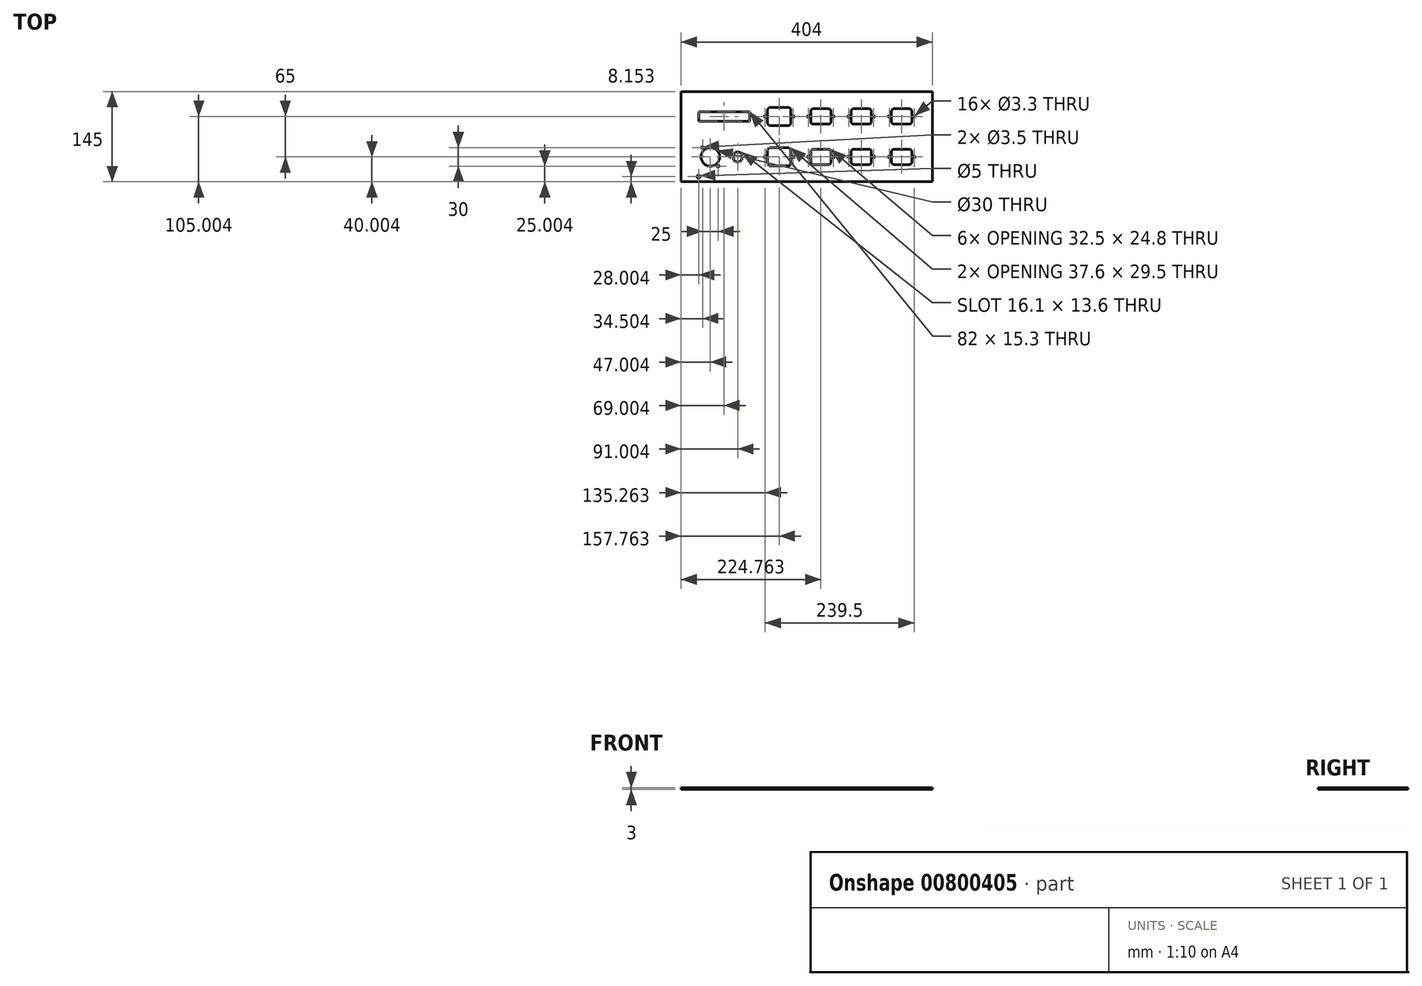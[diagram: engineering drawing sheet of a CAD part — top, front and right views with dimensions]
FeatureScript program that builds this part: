
annotation { "Feature Type Name" : "Feature", "Feature Type Description" : "" }
export const myFeature = defineFeature(function(context is Context, id is Id, definition is map)
    precondition{}
    {
        {
            var Q0;
            Q0=qCreatedBy(makeId("Top.planeOp"),FACE);
            var sketch = newSketch(context, id + "F0", { "sketchPlane" : qUnion([Q0])});
            skLineSegment(sketch, "E0.bottom", {"start": v(-216.19, 64.87) * mm, "end": v(187.81, 64.87) * mm});
            skLineSegment(sketch, "E0.top", {"start": v(-216.19, -80.13) * mm, "end": v(187.81, -80.13) * mm});
            skLineSegment(sketch, "E0.left", {"start": v(-216.19, 64.87) * mm, "end": v(-216.19, -80.13) * mm});
            skLineSegment(sketch, "E0.right", {"start": v(187.81, 64.87) * mm, "end": v(187.81, -80.13) * mm});
            skSolve(sketch);
        }
        {
            var Q0;
            Q0=qCreatedBy(makeId("Top.planeOp"),FACE);
            var sketch = newSketch(context, id + "F1", { "sketchPlane" : qUnion([Q0])});
            skLineSegment(sketch, "E1.bottom", {"start": v(150.82, 12.47) * mm, "end": v(126.32, 12.47) * mm});
            skLineSegment(sketch, "E1.top", {"start": v(150.82, 37.27) * mm, "end": v(126.32, 37.27) * mm});
            skLineSegment(sketch, "E1.left", {"start": v(154.82, 16.47) * mm, "end": v(154.82, 33.27) * mm});
            skLineSegment(sketch, "E1.right", {"start": v(122.32, 16.47) * mm, "end": v(122.32, 33.27) * mm});
            skPoint(sketch, "E1.middle", {"position": v(138.57, 24.87) * mm});
            skPoint(sketch, "E2.visualSharp", {"position": v(122.32, 37.27) * mm});
            skArc(sketch, "E2.filletArc", {"start": v(126.32, 37.27) * mm, "mid": v(123.5, 36.1) * mm, "end": v(122.32, 33.27) * mm});
            skPoint(sketch, "E3.visualSharp", {"position": v(154.82, 37.27) * mm});
            skArc(sketch, "E3.filletArc", {"start": v(154.82, 33.27) * mm, "mid": v(153.65, 36.1) * mm, "end": v(150.82, 37.27) * mm});
            skPoint(sketch, "E4.visualSharp", {"position": v(154.82, 12.47) * mm});
            skArc(sketch, "E4.filletArc", {"start": v(150.82, 12.47) * mm, "mid": v(153.65, 13.65) * mm, "end": v(154.82, 16.47) * mm});
            skPoint(sketch, "E5.visualSharp", {"position": v(122.32, 12.47) * mm});
            skArc(sketch, "E5.filletArc", {"start": v(122.32, 16.47) * mm, "mid": v(123.5, 13.65) * mm, "end": v(126.32, 12.47) * mm});
            skCircle(sketch, "E6", {"center": v(158.57, 24.87) * mm, "radius": 1.5 * mm});
            skCircle(sketch, "E7", {"center": v(118.57, 24.87) * mm, "radius": 1.5 * mm});
            skLineSegment(sketch, "E8.bottom", {"start": v(-44.63, 10.12) * mm, "end": v(-72.23, 10.12) * mm});
            skLineSegment(sketch, "E8.top", {"start": v(-44.63, 39.62) * mm, "end": v(-72.23, 39.62) * mm});
            skLineSegment(sketch, "E8.left", {"start": v(-39.63, 15.12) * mm, "end": v(-39.63, 34.62) * mm});
            skLineSegment(sketch, "E8.right", {"start": v(-77.23, 15.12) * mm, "end": v(-77.23, 34.62) * mm});
            skPoint(sketch, "E8.middle", {"position": v(-58.43, 24.87) * mm});
            skPoint(sketch, "E9.visualSharp", {"position": v(-77.23, 39.62) * mm});
            skArc(sketch, "E9.filletArc", {"start": v(-72.23, 39.62) * mm, "mid": v(-75.76, 38.16) * mm, "end": v(-77.23, 34.62) * mm});
            skPoint(sketch, "E10.visualSharp", {"position": v(-39.63, 39.62) * mm});
            skArc(sketch, "E10.filletArc", {"start": v(-39.63, 34.62) * mm, "mid": v(-41.1, 38.16) * mm, "end": v(-44.63, 39.62) * mm});
            skPoint(sketch, "E11.visualSharp", {"position": v(-39.63, 10.12) * mm});
            skArc(sketch, "E11.filletArc", {"start": v(-44.63, 10.12) * mm, "mid": v(-41.1, 11.59) * mm, "end": v(-39.63, 15.12) * mm});
            skPoint(sketch, "E12.visualSharp", {"position": v(-77.23, 10.12) * mm});
            skArc(sketch, "E12.filletArc", {"start": v(-77.23, 15.12) * mm, "mid": v(-75.76, 11.59) * mm, "end": v(-72.23, 10.12) * mm});
            skCircle(sketch, "E13", {"center": v(-35.93, 24.87) * mm, "radius": 1.5 * mm});
            skCircle(sketch, "E14", {"center": v(-80.93, 24.87) * mm, "radius": 1.5 * mm});
            skLineSegment(sketch, "E15", {"start": v(-85.43, 7.87) * mm, "end": v(-85.43, 41.87) * mm, "construction": true});
            skLineSegment(sketch, "E16", {"start": v(-85.43, 41.87) * mm, "end": v(-31.43, 41.87) * mm, "construction": true});
            skLineSegment(sketch, "E17", {"start": v(-31.43, 41.87) * mm, "end": v(-31.43, 7.87) * mm, "construction": true});
            skLineSegment(sketch, "E18", {"start": v(-31.43, 7.87) * mm, "end": v(-85.43, 7.87) * mm, "construction": true});
            skLineSegment(sketch, "E19", {"start": v(113.57, 38.87) * mm, "end": v(113.57, 10.87) * mm, "construction": true});
            skLineSegment(sketch, "E20", {"start": v(113.57, 10.87) * mm, "end": v(163.57, 10.87) * mm, "construction": true});
            skLineSegment(sketch, "E21", {"start": v(163.57, 10.87) * mm, "end": v(163.57, 38.87) * mm, "construction": true});
            skLineSegment(sketch, "E22", {"start": v(163.57, 38.87) * mm, "end": v(113.57, 38.87) * mm, "construction": true});
            skLineSegment(sketch, "E23.0.1.0", {"start": v(163.57, -26.13) * mm, "end": v(113.57, -26.13) * mm, "construction": true});
            skLineSegment(sketch, "E23.0.1.1", {"start": v(113.57, -26.13) * mm, "end": v(113.57, -54.13) * mm, "construction": true});
            skLineSegment(sketch, "E23.0.1.2", {"start": v(163.57, -54.13) * mm, "end": v(163.57, -26.13) * mm, "construction": true});
            skLineSegment(sketch, "E23.0.1.3", {"start": v(122.32, -48.53) * mm, "end": v(122.32, -31.73) * mm});
            skLineSegment(sketch, "E23.0.1.4", {"start": v(154.82, -48.53) * mm, "end": v(154.82, -31.73) * mm});
            skLineSegment(sketch, "E23.0.1.5", {"start": v(150.82, -27.73) * mm, "end": v(126.32, -27.73) * mm});
            skPoint(sketch, "E23.0.1.6", {"position": v(154.82, -27.73) * mm});
            skLineSegment(sketch, "E23.0.1.7", {"start": v(150.82, -52.53) * mm, "end": v(126.32, -52.53) * mm});
            skLineSegment(sketch, "E23.0.1.8", {"start": v(113.57, -54.13) * mm, "end": v(163.57, -54.13) * mm, "construction": true});
            skPoint(sketch, "E23.0.1.9", {"position": v(138.57, -40.13) * mm});
            skPoint(sketch, "E23.0.1.10", {"position": v(122.32, -52.53) * mm});
            skPoint(sketch, "E23.0.1.11", {"position": v(154.82, -52.53) * mm});
            skPoint(sketch, "E23.0.1.12", {"position": v(122.32, -27.73) * mm});
            skCircle(sketch, "E23.0.1.13", {"center": v(158.57, -40.13) * mm, "radius": 1.5 * mm});
            skCircle(sketch, "E23.0.1.14", {"center": v(118.57, -40.13) * mm, "radius": 1.5 * mm});
            skArc(sketch, "E23.0.1.15", {"start": v(122.32, -48.53) * mm, "mid": v(123.5, -51.35) * mm, "end": v(126.32, -52.53) * mm});
            skArc(sketch, "E23.0.1.16", {"start": v(154.82, -31.73) * mm, "mid": v(153.65, -28.9) * mm, "end": v(150.82, -27.73) * mm});
            skArc(sketch, "E23.0.1.17", {"start": v(150.82, -52.53) * mm, "mid": v(153.65, -51.35) * mm, "end": v(154.82, -48.53) * mm});
            skArc(sketch, "E23.0.1.18", {"start": v(126.32, -27.73) * mm, "mid": v(123.5, -28.9) * mm, "end": v(122.32, -31.73) * mm});
            skLineSegment(sketch, "E23.1.0.0", {"start": v(98.57, 38.87) * mm, "end": v(48.57, 38.87) * mm, "construction": true});
            skLineSegment(sketch, "E23.1.0.1", {"start": v(48.57, 38.87) * mm, "end": v(48.57, 10.87) * mm, "construction": true});
            skLineSegment(sketch, "E23.1.0.2", {"start": v(98.57, 10.87) * mm, "end": v(98.57, 38.87) * mm, "construction": true});
            skLineSegment(sketch, "E23.1.0.3", {"start": v(57.32, 16.47) * mm, "end": v(57.32, 33.27) * mm});
            skLineSegment(sketch, "E23.1.0.4", {"start": v(89.82, 16.47) * mm, "end": v(89.82, 33.27) * mm});
            skLineSegment(sketch, "E23.1.0.5", {"start": v(85.82, 37.27) * mm, "end": v(61.32, 37.27) * mm});
            skPoint(sketch, "E23.1.0.6", {"position": v(89.82, 37.27) * mm});
            skLineSegment(sketch, "E23.1.0.7", {"start": v(85.82, 12.47) * mm, "end": v(61.32, 12.47) * mm});
            skLineSegment(sketch, "E23.1.0.8", {"start": v(48.57, 10.87) * mm, "end": v(98.57, 10.87) * mm, "construction": true});
            skPoint(sketch, "E23.1.0.9", {"position": v(73.57, 24.87) * mm});
            skPoint(sketch, "E23.1.0.10", {"position": v(57.32, 12.47) * mm});
            skPoint(sketch, "E23.1.0.11", {"position": v(89.82, 12.47) * mm});
            skPoint(sketch, "E23.1.0.12", {"position": v(57.32, 37.27) * mm});
            skCircle(sketch, "E23.1.0.13", {"center": v(93.57, 24.87) * mm, "radius": 1.5 * mm});
            skCircle(sketch, "E23.1.0.14", {"center": v(53.57, 24.87) * mm, "radius": 1.5 * mm});
            skArc(sketch, "E23.1.0.15", {"start": v(57.32, 16.47) * mm, "mid": v(58.5, 13.65) * mm, "end": v(61.32, 12.47) * mm});
            skArc(sketch, "E23.1.0.16", {"start": v(89.82, 33.27) * mm, "mid": v(88.65, 36.1) * mm, "end": v(85.82, 37.27) * mm});
            skArc(sketch, "E23.1.0.17", {"start": v(85.82, 12.47) * mm, "mid": v(88.65, 13.65) * mm, "end": v(89.82, 16.47) * mm});
            skArc(sketch, "E23.1.0.18", {"start": v(61.32, 37.27) * mm, "mid": v(58.5, 36.1) * mm, "end": v(57.32, 33.27) * mm});
            skLineSegment(sketch, "E23.1.1.0", {"start": v(98.57, -26.13) * mm, "end": v(48.57, -26.13) * mm, "construction": true});
            skLineSegment(sketch, "E23.1.1.1", {"start": v(48.57, -26.13) * mm, "end": v(48.57, -54.13) * mm, "construction": true});
            skLineSegment(sketch, "E23.1.1.2", {"start": v(98.57, -54.13) * mm, "end": v(98.57, -26.13) * mm, "construction": true});
            skLineSegment(sketch, "E23.1.1.3", {"start": v(57.32, -48.53) * mm, "end": v(57.32, -31.73) * mm});
            skLineSegment(sketch, "E23.1.1.4", {"start": v(89.82, -48.53) * mm, "end": v(89.82, -31.73) * mm});
            skLineSegment(sketch, "E23.1.1.5", {"start": v(85.82, -27.73) * mm, "end": v(61.32, -27.73) * mm});
            skPoint(sketch, "E23.1.1.6", {"position": v(89.82, -27.73) * mm});
            skLineSegment(sketch, "E23.1.1.7", {"start": v(85.82, -52.53) * mm, "end": v(61.32, -52.53) * mm});
            skLineSegment(sketch, "E23.1.1.8", {"start": v(48.57, -54.13) * mm, "end": v(98.57, -54.13) * mm, "construction": true});
            skPoint(sketch, "E23.1.1.9", {"position": v(73.57, -40.13) * mm});
            skPoint(sketch, "E23.1.1.10", {"position": v(57.32, -52.53) * mm});
            skPoint(sketch, "E23.1.1.11", {"position": v(89.82, -52.53) * mm});
            skPoint(sketch, "E23.1.1.12", {"position": v(57.32, -27.73) * mm});
            skCircle(sketch, "E23.1.1.13", {"center": v(93.57, -40.13) * mm, "radius": 1.5 * mm});
            skCircle(sketch, "E23.1.1.14", {"center": v(53.57, -40.13) * mm, "radius": 1.5 * mm});
            skArc(sketch, "E23.1.1.15", {"start": v(57.32, -48.53) * mm, "mid": v(58.5, -51.35) * mm, "end": v(61.32, -52.53) * mm});
            skArc(sketch, "E23.1.1.16", {"start": v(89.82, -31.73) * mm, "mid": v(88.65, -28.9) * mm, "end": v(85.82, -27.73) * mm});
            skArc(sketch, "E23.1.1.17", {"start": v(85.82, -52.53) * mm, "mid": v(88.65, -51.35) * mm, "end": v(89.82, -48.53) * mm});
            skArc(sketch, "E23.1.1.18", {"start": v(61.32, -27.73) * mm, "mid": v(58.5, -28.9) * mm, "end": v(57.32, -31.73) * mm});
            skLineSegment(sketch, "E23.2.0.0", {"start": v(33.57, 38.87) * mm, "end": v(-16.43, 38.87) * mm, "construction": true});
            skLineSegment(sketch, "E23.2.0.1", {"start": v(-16.43, 38.87) * mm, "end": v(-16.43, 10.87) * mm, "construction": true});
            skLineSegment(sketch, "E23.2.0.2", {"start": v(33.57, 10.87) * mm, "end": v(33.57, 38.87) * mm, "construction": true});
            skLineSegment(sketch, "E23.2.0.3", {"start": v(-7.68, 16.47) * mm, "end": v(-7.68, 33.27) * mm});
            skLineSegment(sketch, "E23.2.0.4", {"start": v(24.82, 16.47) * mm, "end": v(24.82, 33.27) * mm});
            skLineSegment(sketch, "E23.2.0.5", {"start": v(20.82, 37.27) * mm, "end": v(-3.68, 37.27) * mm});
            skPoint(sketch, "E23.2.0.6", {"position": v(24.82, 37.27) * mm});
            skLineSegment(sketch, "E23.2.0.7", {"start": v(20.82, 12.47) * mm, "end": v(-3.68, 12.47) * mm});
            skLineSegment(sketch, "E23.2.0.8", {"start": v(-16.43, 10.87) * mm, "end": v(33.57, 10.87) * mm, "construction": true});
            skPoint(sketch, "E23.2.0.9", {"position": v(8.57, 24.87) * mm});
            skPoint(sketch, "E23.2.0.10", {"position": v(-7.68, 12.47) * mm});
            skPoint(sketch, "E23.2.0.11", {"position": v(24.82, 12.47) * mm});
            skPoint(sketch, "E23.2.0.12", {"position": v(-7.68, 37.27) * mm});
            skCircle(sketch, "E23.2.0.13", {"center": v(28.57, 24.87) * mm, "radius": 1.5 * mm});
            skCircle(sketch, "E23.2.0.14", {"center": v(-11.43, 24.87) * mm, "radius": 1.5 * mm});
            skArc(sketch, "E23.2.0.15", {"start": v(-7.68, 16.47) * mm, "mid": v(-6.5, 13.65) * mm, "end": v(-3.68, 12.47) * mm});
            skArc(sketch, "E23.2.0.16", {"start": v(24.82, 33.27) * mm, "mid": v(23.65, 36.1) * mm, "end": v(20.82, 37.27) * mm});
            skArc(sketch, "E23.2.0.17", {"start": v(20.82, 12.47) * mm, "mid": v(23.65, 13.65) * mm, "end": v(24.82, 16.47) * mm});
            skArc(sketch, "E23.2.0.18", {"start": v(-3.68, 37.27) * mm, "mid": v(-6.5, 36.1) * mm, "end": v(-7.68, 33.27) * mm});
            skLineSegment(sketch, "E23.2.1.0", {"start": v(33.57, -26.13) * mm, "end": v(-16.43, -26.13) * mm, "construction": true});
            skLineSegment(sketch, "E23.2.1.1", {"start": v(-16.43, -26.13) * mm, "end": v(-16.43, -54.13) * mm, "construction": true});
            skLineSegment(sketch, "E23.2.1.2", {"start": v(33.57, -54.13) * mm, "end": v(33.57, -26.13) * mm, "construction": true});
            skLineSegment(sketch, "E23.2.1.3", {"start": v(-7.68, -48.53) * mm, "end": v(-7.68, -31.73) * mm});
            skLineSegment(sketch, "E23.2.1.4", {"start": v(24.82, -48.53) * mm, "end": v(24.82, -31.73) * mm});
            skLineSegment(sketch, "E23.2.1.5", {"start": v(20.82, -27.73) * mm, "end": v(-3.68, -27.73) * mm});
            skPoint(sketch, "E23.2.1.6", {"position": v(24.82, -27.73) * mm});
            skLineSegment(sketch, "E23.2.1.7", {"start": v(20.82, -52.53) * mm, "end": v(-3.68, -52.53) * mm});
            skLineSegment(sketch, "E23.2.1.8", {"start": v(-16.43, -54.13) * mm, "end": v(33.57, -54.13) * mm, "construction": true});
            skPoint(sketch, "E23.2.1.9", {"position": v(8.57, -40.13) * mm});
            skPoint(sketch, "E23.2.1.10", {"position": v(-7.68, -52.53) * mm});
            skPoint(sketch, "E23.2.1.11", {"position": v(24.82, -52.53) * mm});
            skPoint(sketch, "E23.2.1.12", {"position": v(-7.68, -27.73) * mm});
            skCircle(sketch, "E23.2.1.13", {"center": v(28.57, -40.13) * mm, "radius": 1.5 * mm});
            skCircle(sketch, "E23.2.1.14", {"center": v(-11.43, -40.13) * mm, "radius": 1.5 * mm});
            skArc(sketch, "E23.2.1.15", {"start": v(-7.68, -48.53) * mm, "mid": v(-6.5, -51.35) * mm, "end": v(-3.68, -52.53) * mm});
            skArc(sketch, "E23.2.1.16", {"start": v(24.82, -31.73) * mm, "mid": v(23.65, -28.9) * mm, "end": v(20.82, -27.73) * mm});
            skArc(sketch, "E23.2.1.17", {"start": v(20.82, -52.53) * mm, "mid": v(23.65, -51.35) * mm, "end": v(24.82, -48.53) * mm});
            skArc(sketch, "E23.2.1.18", {"start": v(-3.68, -27.73) * mm, "mid": v(-6.5, -28.9) * mm, "end": v(-7.68, -31.73) * mm});
            skLineSegment(sketch, "E23.direction1", {"start": v(113.57, 10.87) * mm, "end": v(48.57, 10.87) * mm, "construction": true});
            skLineSegment(sketch, "E23.direction2", {"start": v(113.57, 10.87) * mm, "end": v(113.57, -54.13) * mm, "construction": true});
            skPoint(sketch, "E24.0.1.0", {"position": v(-77.23, -54.88) * mm});
            skPoint(sketch, "E24.0.1.1", {"position": v(-39.63, -54.88) * mm});
            skLineSegment(sketch, "E24.0.1.2", {"start": v(-85.43, -23.13) * mm, "end": v(-31.43, -23.13) * mm, "construction": true});
            skLineSegment(sketch, "E24.0.1.3", {"start": v(-31.43, -23.13) * mm, "end": v(-31.43, -57.13) * mm, "construction": true});
            skPoint(sketch, "E24.0.1.4", {"position": v(-58.43, -40.13) * mm});
            skLineSegment(sketch, "E24.0.1.5", {"start": v(-31.43, -57.13) * mm, "end": v(-85.43, -57.13) * mm, "construction": true});
            skLineSegment(sketch, "E24.0.1.6", {"start": v(-77.23, -49.88) * mm, "end": v(-77.23, -30.38) * mm});
            skLineSegment(sketch, "E24.0.1.7", {"start": v(-85.43, -57.13) * mm, "end": v(-85.43, -23.13) * mm, "construction": true});
            skPoint(sketch, "E24.0.1.8", {"position": v(-77.23, -25.38) * mm});
            skLineSegment(sketch, "E24.0.1.9", {"start": v(-39.63, -49.88) * mm, "end": v(-39.63, -30.38) * mm});
            skLineSegment(sketch, "E24.0.1.10", {"start": v(-44.63, -54.88) * mm, "end": v(-72.23, -54.88) * mm});
            skLineSegment(sketch, "E24.0.1.11", {"start": v(-44.63, -25.38) * mm, "end": v(-72.23, -25.38) * mm});
            skPoint(sketch, "E24.0.1.12", {"position": v(-39.63, -25.38) * mm});
            skCircle(sketch, "E24.0.1.13", {"center": v(-35.93, -40.13) * mm, "radius": 1.5 * mm});
            skArc(sketch, "E24.0.1.14", {"start": v(-72.23, -25.38) * mm, "mid": v(-75.76, -26.84) * mm, "end": v(-77.23, -30.38) * mm});
            skArc(sketch, "E24.0.1.15", {"start": v(-77.23, -49.88) * mm, "mid": v(-75.76, -53.41) * mm, "end": v(-72.23, -54.88) * mm});
            skCircle(sketch, "E24.0.1.16", {"center": v(-80.93, -40.13) * mm, "radius": 1.5 * mm});
            skArc(sketch, "E24.0.1.17", {"start": v(-44.63, -54.88) * mm, "mid": v(-41.1, -53.41) * mm, "end": v(-39.63, -49.88) * mm});
            skArc(sketch, "E24.0.1.18", {"start": v(-39.63, -30.38) * mm, "mid": v(-41.1, -26.84) * mm, "end": v(-44.63, -25.38) * mm});
            skLineSegment(sketch, "E24.direction1", {"start": v(-85.43, 7.87) * mm, "end": v(-79.08, 7.87) * mm, "construction": true});
            skLineSegment(sketch, "E24.direction2", {"start": v(-85.43, 7.87) * mm, "end": v(-85.43, -57.13) * mm, "construction": true});
            skCircle(sketch, "E25", {"center": v(-169.19, -40.13) * mm, "radius": 15 * mm});
            skCircle(sketch, "E26", {"center": v(-156.69, -55.13) * mm, "radius": 1.75 * mm});
            skCircle(sketch, "E27", {"center": v(-181.69, -25.13) * mm, "radius": 1.75 * mm});
            skLineSegment(sketch, "E28.bottom", {"start": v(-106.19, 17.22) * mm, "end": v(-188.19, 17.22) * mm});
            skLineSegment(sketch, "E28.top", {"start": v(-106.19, 32.52) * mm, "end": v(-188.19, 32.52) * mm});
            skLineSegment(sketch, "E28.left", {"start": v(-106.19, 17.22) * mm, "end": v(-106.19, 32.52) * mm});
            skLineSegment(sketch, "E28.right", {"start": v(-188.19, 17.22) * mm, "end": v(-188.19, 32.52) * mm});
            skPoint(sketch, "E28.middle", {"position": v(-147.19, 24.87) * mm});
            skPoint(sketch, "E29", {"position": v(-147.19, 17.22) * mm});
            skCircle(sketch, "E30", {"center": v(-188.19, -71.98) * mm, "radius": 2.5 * mm});
            skArc(sketch, "E31", {"start": v(-131.99, -44.43) * mm, "mid": v(-125.19, -48.18) * mm, "end": v(-118.39, -44.43) * mm});
            skLineSegment(sketch, "E32", {"start": v(-131.99, -35.82) * mm, "end": v(-131.99, -44.43) * mm});
            skLineSegment(sketch, "E33", {"start": v(-118.39, -35.82) * mm, "end": v(-118.39, -44.43) * mm});
            skArc(sketch, "E34.trimOffspring", {"start": v(-118.39, -35.82) * mm, "mid": v(-125.19, -32.08) * mm, "end": v(-131.99, -35.82) * mm});
            skSolve(sketch);
        }
        {
            var Q0;
            Q0=makeQuery(id+"F0.imprint","IMPRINT",FACE,{"disambiguationData":[TD([[makeQuery(id+"F0.imprint","IMPRINT",EDGE,{"derivedFrom":sQuery(id+"F0.wireOp",EDGE,"E0.bottom")}),-1.0]])]});
            extrude(context, id + "F2", {"entities" : qUnion([Q0]), "oppositeDirection" : true, "depth" : 3 * mm, "offsetDistance" : 25 * mm});
        }
        {
            var Q0;
            Q0=sQuery(id+"F1.wireOp",VERTEX,"E7.center");
            var Q1;
            Q1=sQuery(id+"F1.wireOp",VERTEX,"E6.center");
            var Q2;
            Q2=sQuery(id+"F1.wireOp",VERTEX,"E23.1.0.13.center");
            var Q3;
            Q3=sQuery(id+"F1.wireOp",VERTEX,"E23.1.0.14.center");
            var Q4;
            Q4=sQuery(id+"F1.wireOp",VERTEX,"E23.1.1.14.center");
            var Q5;
            Q5=sQuery(id+"F1.wireOp",VERTEX,"E23.1.1.13.center");
            var Q6;
            Q6=sQuery(id+"F1.wireOp",VERTEX,"E23.0.1.14.center");
            var Q7;
            Q7=sQuery(id+"F1.wireOp",VERTEX,"E23.0.1.13.center");
            var Q8;
            Q8=sQuery(id+"F1.wireOp",VERTEX,"E23.2.1.13.center");
            var Q9;
            Q9=sQuery(id+"F1.wireOp",VERTEX,"E23.2.1.14.center");
            var Q10;
            Q10=sQuery(id+"F1.wireOp",VERTEX,"E23.2.0.14.center");
            var Q11;
            Q11=sQuery(id+"F1.wireOp",VERTEX,"E23.2.0.13.center");
            var Q12;
            Q12=sQuery(id+"F1.wireOp",VERTEX,"E13.center");
            var Q13;
            Q13=sQuery(id+"F1.wireOp",VERTEX,"E14.center");
            var Q14;
            Q14=sQuery(id+"F1.wireOp",VERTEX,"E24.0.1.16.center");
            var Q15;
            Q15=sQuery(id+"F1.wireOp",VERTEX,"E24.0.1.13.center");
            var Q16;
            Q16=makeQuery(id+"F2.opExtrude","SWEPT_BODY",BODY,{"disambiguationData":[OSD([sQuery(id+"F0.wireOp",EDGE,"E0.bottom"),sQuery(id+"F0.wireOp",EDGE,"E0.top"),sQuery(id+"F0.wireOp",EDGE,"E0.left"),sQuery(id+"F0.wireOp",EDGE,"E0.right")])]});
            hole(context, id + "F3", {"style" : HoleStyle.SIMPLE, "endStyle" : HoleEndStyle.BLIND, "standardTappedOrClearance" : lookupTablePath({ "standard" : "ISO", "engagement" : "75%", "pitch" : "0.7 mm", "size" : "M4", "type" : "Tapped" }), "standardBlindInLast" : lookupTablePath({ "standard" : "ISO", "engagement" : "75%", "pitch" : "0.7 mm", "size" : "M4", "type" : "Tapped" }), "holeDiameter" : 3.3 * mm, "majorDiameter" : 4 * mm, "showTappedDepth" : true, "holeDepth" : 8.6 * mm, "isTappedThrough" : true, "tappedDepth" : 6.5 * mm, "tapClearance" : 3, "locations" : qUnion([Q0, Q1, Q2, Q3, Q4, Q5, Q6, Q7, Q8, Q9, Q10, Q11, Q12, Q13, Q14, Q15]), "scope" : qUnion([Q16])});
        }
        {
            var Q0;
            Q0=qSketchRegion(id+"F1",true);
            extrude(context, id + "F4", {"entities" : qUnion([Q0]), "operationType" : NewBodyOperationType.REMOVE, "oppositeDirection" : true, "depth" : 25 * mm, "offsetDistance" : 25 * mm});
        }
    });
